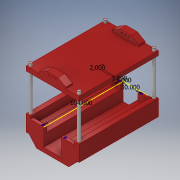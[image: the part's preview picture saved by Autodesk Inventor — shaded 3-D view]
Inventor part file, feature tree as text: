
AUTODESK INVENTOR PART (.ipt)
format: ipt  version: 2018 (Build 220112000, 112)  size: 1,002,496 bytes
history: native  units: in
note: dims shown in document units (in); Inventor stores cm internally (conversion verified against a paired STEP export)
features: sketch x9, extrude x8, projected_geometry x5, other x2, shell x1
ambient origin geometry x8: Origin, YZ Plane, XZ Plane, XY Plane, X Axis, Y Axis, Z Axis, Center Point
bodies: Solid1 (feature_tree)
feature tree (25):
  extrude  "Extrusion1"  Depth=22.0in
  extrude  "Extrusion2"  Depth=76.0in
  extrude  "Extrusion4"  Depth=20.0in
  shell  "Shell2"  Thickness=2.0in
  extrude  "Extrusion5"  Depth=44.0in
  extrude  "Extrusion6"  Depth=24.0in
  extrude  "Extrusion7"  Depth=108.0in TaperAngle=0.0deg
  extrude  "Extrusion9"  Depth=8.0in TaperAngle=0.0deg
  extrude  "Extrusion8"  Depth=6.0in
  sketch  "Sketch10"  dims[d109=2.0in d110=19.0in d111=108.0in d112=0.0in d114=90.0in d115=2.0in d117=72.0in d118=2.0in d119=8.0in d120=30.0deg d121=36.0in d122=2.0in d123=3.0in d124=2.0in d125=2.0in d126=4.5in d127=4.5in d128=3.0in d129=108.0in d130=0.0in d131=45.0in d132=24.0in d133=0.0in d134=2.0in d135=24.0in d136=0.0in d138=19.0in d139=4.0in d140=3.0in d141=3.0in d142=0.7874in d144=66.0in d145=0.7874in d147=102.0in d150=60.0in d151=0.0in d152=2.0in d153=60.0in d154=0.0in d155=1.0in d158=3.0in d159=3.0in d160=2.0in d161=0.7874in d163=30.0in d164=0.3937in d166=1.0in d168=0.7874in d170=104.0in d171=0.3937in d173=1.0in]
  sketch  "Sketch1"  dims[d9=0.8933in d27=22.0in]
  other  "Image1"
  sketch  "Sketch2"  dims[d29=72.0in d30=76.0in]
  projected_geometry  "Projected Loop1"
  projected_geometry  "Projected Loop2"
  sketch  "Sketch4"  dims[d37=4.0in d46=20.0in d47=2.0in]
  other  "Image2"
  sketch  "Sketch5"  dims[d51=6.0in d68=44.0in]
  sketch  "Sketch6"  dims[d69=12.0in d74=24.0in]
  projected_geometry  "Projected Loop3"
  projected_geometry  "Projected Loop4"
  sketch  "Sketch7"  dims[d77=24.0in d78=108.0in d79=0.0in]
  projected_geometry  "Projected Loop5"
  sketch  "Sketch8"  dims[d80=100.0in d81=8.0in d82=0.0in]
  sketch  "Sketch9"  dims[d98=76.0in d107=6.0in]
